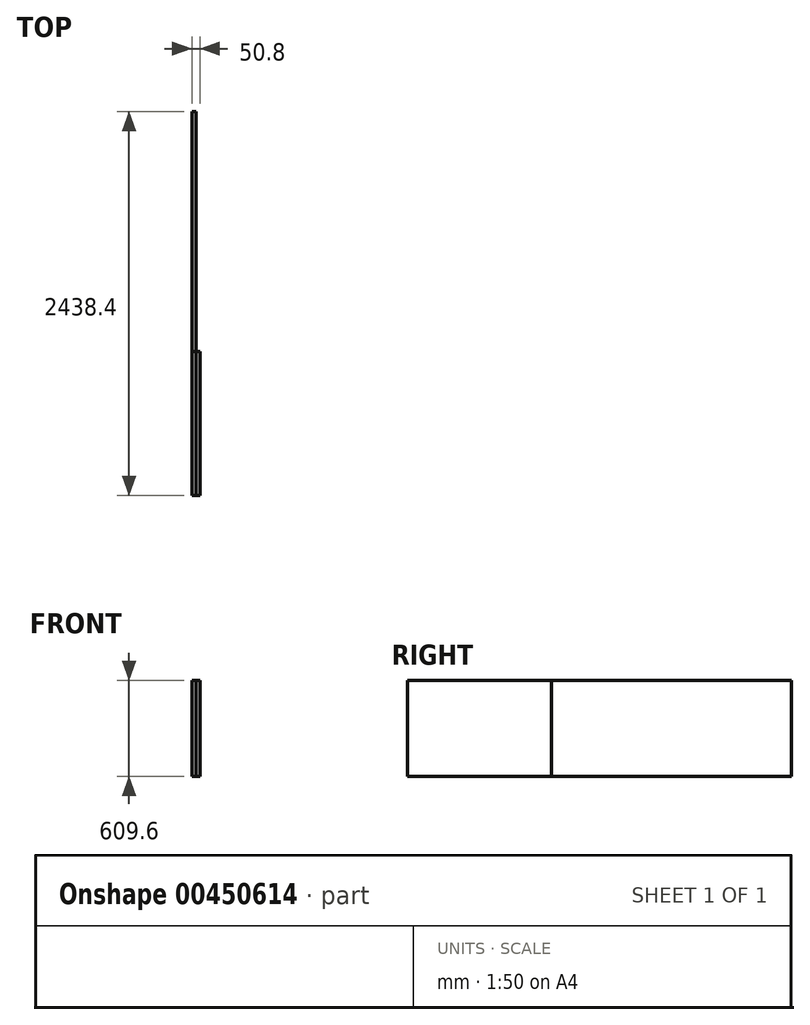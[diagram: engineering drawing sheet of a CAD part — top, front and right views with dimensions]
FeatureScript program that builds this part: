
annotation { "Feature Type Name" : "Feature", "Feature Type Description" : "" }
export const myFeature = defineFeature(function(context is Context, id is Id, definition is map)
    precondition{}
    {
        {
            var Q0;
            Q0=qCreatedBy(makeId("Right.planeOp"),FACE);
            var sketch = newSketch(context, id + "F0", { "sketchPlane" : qUnion([Q0])});
            skLineSegment(sketch, "E0.bottom", {"start": v(0, 0) * mm, "end": v(2438.4, 0) * mm});
            skLineSegment(sketch, "E0.top", {"start": v(0, 609.6) * mm, "end": v(2438.4, 609.6) * mm});
            skLineSegment(sketch, "E0.left", {"start": v(0, 0) * mm, "end": v(0, 609.6) * mm});
            skLineSegment(sketch, "E0.right", {"start": v(2438.4, 0) * mm, "end": v(2438.4, 609.6) * mm});
            skSolve(sketch);
        }
        {
            var Q0;
            Q0 = qSketchRegion(id + "F0", true);
            extrude(context, id + "F1", {"entities" : qUnion([Q0]), "depth" : 25.4 * mm, "offsetDistance" : 25.4 * mm});
        }
        {
            var Q0;
            Q0=qCreatedBy(makeId("Right.planeOp"),FACE);
            var sketch = newSketch(context, id + "F2", { "sketchPlane" : qUnion([Q0])});
            skLineSegment(sketch, "E1.bottom", {"start": v(0, 0) * mm, "end": v(914.4, 0) * mm});
            skLineSegment(sketch, "E1.top", {"start": v(0, 609.6) * mm, "end": v(914.4, 609.6) * mm});
            skLineSegment(sketch, "E1.left", {"start": v(0, 0) * mm, "end": v(0, 609.6) * mm});
            skLineSegment(sketch, "E1.right", {"start": v(914.4, 0) * mm, "end": v(914.4, 609.6) * mm});
            skSolve(sketch);
        }
        {
            var Q0;
            Q0 = qSketchRegion(id + "F2", true);
            extrude(context, id + "F3", {"entities" : qUnion([Q0]), "depth" : 50.8 * mm, "offsetDistance" : 25.4 * mm});
        }
    });
